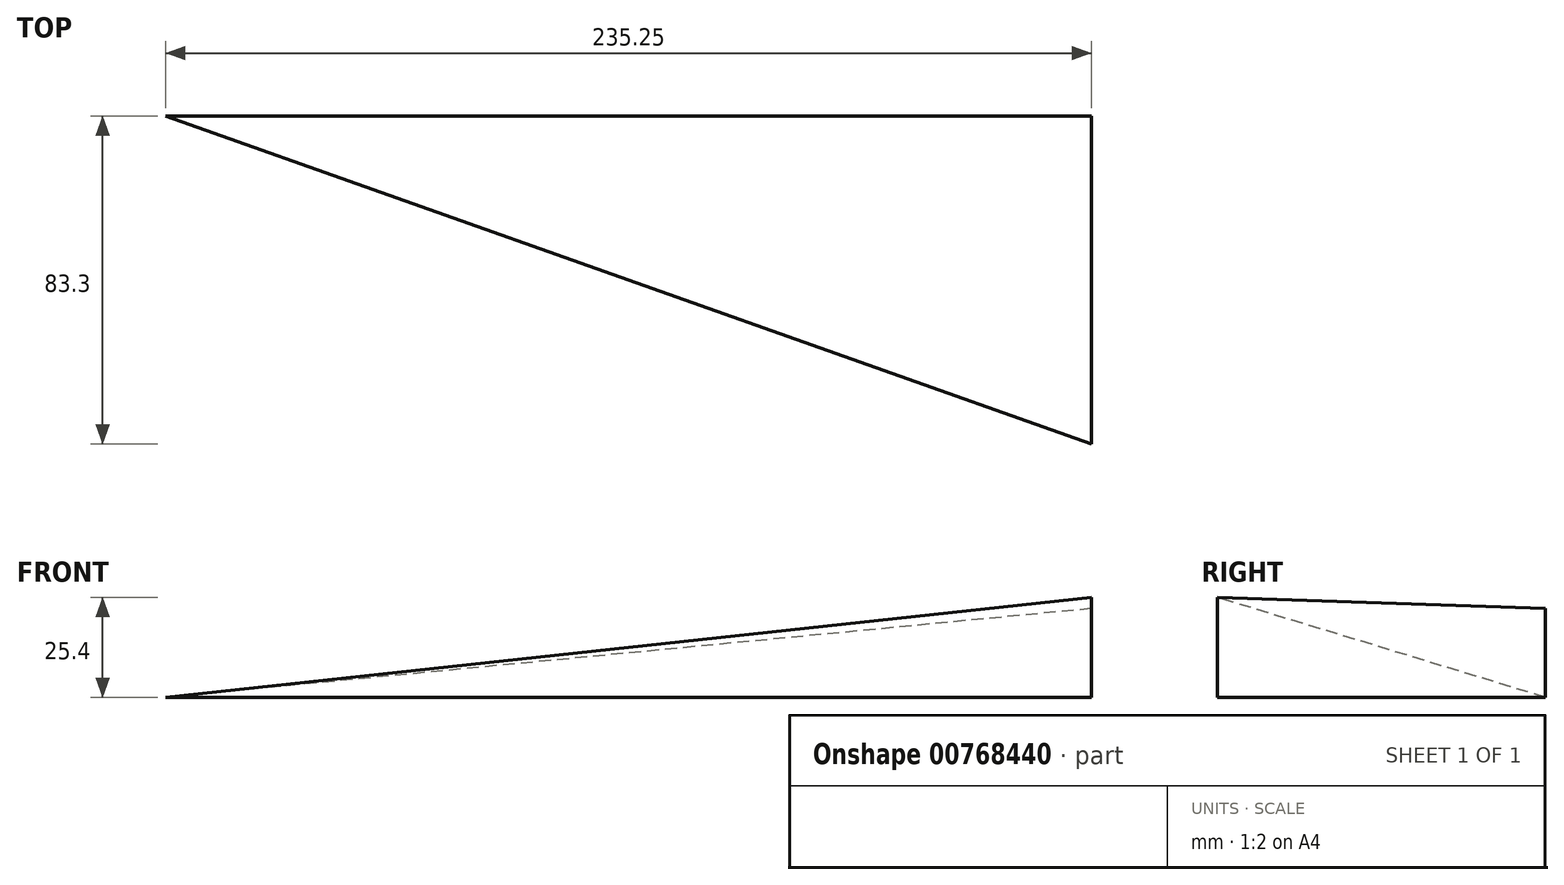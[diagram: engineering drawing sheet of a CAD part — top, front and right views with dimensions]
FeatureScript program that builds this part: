
annotation { "Feature Type Name" : "Feature", "Feature Type Description" : "" }
export const myFeature = defineFeature(function(context is Context, id is Id, definition is map)
    precondition{}
    {
        {
            var Q0;
            Q0=qCreatedBy(makeId("Top.planeOp"),FACE);
            var sketch = newSketch(context, id + "F0", { "sketchPlane" : qUnion([Q0])});
            skLineSegment(sketch, "E0", {"start": v(-135.39, 56.3) * mm, "end": v(99.86, 56.3) * mm});
            skLineSegment(sketch, "E1", {"start": v(99.86, 56.3) * mm, "end": v(99.86, -27) * mm});
            skLineSegment(sketch, "E2", {"start": v(99.86, -27) * mm, "end": v(-135.39, 56.3) * mm});
            skSolve(sketch);
        }
        {
            var Q0;
            Q0=makeQuery(id+"F0.imprint","IMPRINT",FACE,{"disambiguationData":[TD([[makeQuery(id+"F0.imprint","IMPRINT",EDGE,{"derivedFrom":sQuery(id+"F0.wireOp",EDGE,"E0")}),-1.0]])]});
            extrude(context, id + "F1", {"entities" : qUnion([Q0]), "depth" : 25.4 * mm, "offsetDistance" : 25.4 * mm});
        }
        {
            var Q0;
            Q0=makeQuery(id+"F1.opExtrude","SWEPT_FACE",FACE,{"disambiguationData":[OSD([sQuery(id+"F0.wireOp",EDGE,"E2")])]});
            var sketch = newSketch(context, id + "F2", { "sketchPlane" : qUnion([Q0])});
            skLineSegment(sketch, "E3", {"start": v(-146.42, 0) * mm, "end": v(103.14, 25.4) * mm});
            skSolve(sketch);
        }
        {
            var Q0;
            Q0 = qSketchRegion(id + "F2", true);
            var Q1;
            Q1=makeQuery(id+"F2.imprint","IMPRINT",FACE,{"disambiguationData":[TD([[makeQuery(id+"F2.imprint","IMPRINT",EDGE,{"derivedFrom":sQuery(id+"F2.wireOp",EDGE,"E3")}),1.0]])]});
            extrude(context, id + "F3", {"entities" : qUnion([Q0, Q1]), "operationType" : NewBodyOperationType.REMOVE, "oppositeDirection" : true, "depth" : 117.1 * mm, "offsetDistance" : 25.4 * mm});
        }
    });
